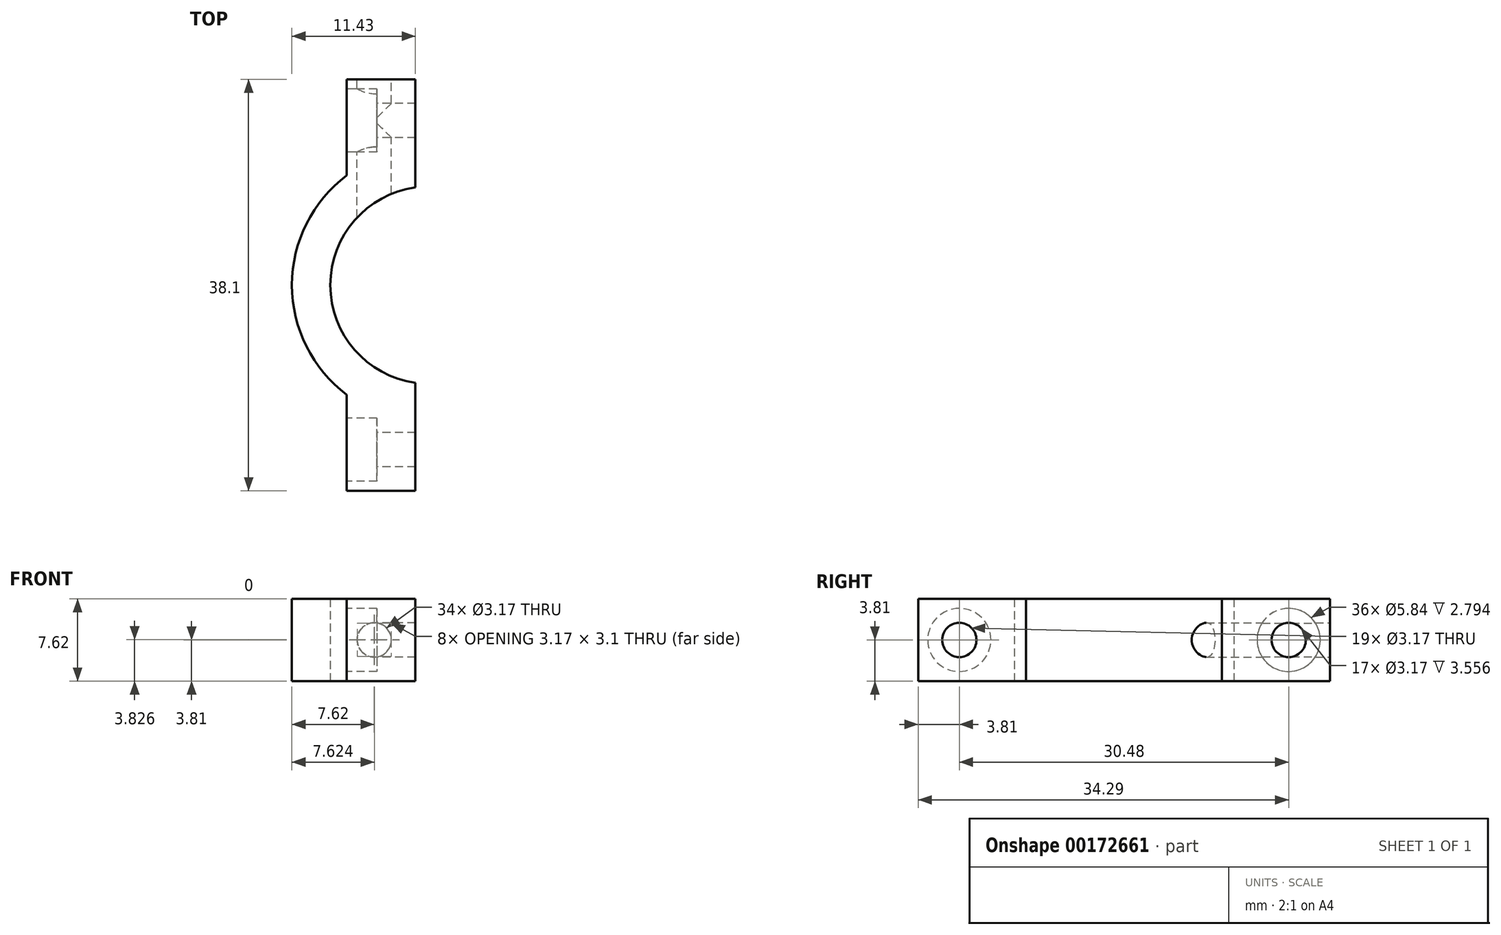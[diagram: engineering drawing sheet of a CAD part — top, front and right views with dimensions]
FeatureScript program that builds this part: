
annotation { "Feature Type Name" : "Feature", "Feature Type Description" : "" }
export const myFeature = defineFeature(function(context is Context, id is Id, definition is map)
    precondition{}
    {
        {
            var Q0;
            Q0=qCreatedBy(makeId("Top.planeOp"),FACE);
            var sketch = newSketch(context, id + "F0", { "sketchPlane" : qUnion([Q0])});
            skArc(sketch, "E0", {"start": v(12.64, 1.27) * mm, "mid": v(0, 12.7) * mm, "end": v(-12.64, 1.27) * mm});
            skArc(sketch, "E1", {"start": v(9.06, 1.27) * mm, "mid": v(0, 9.14) * mm, "end": v(-9.06, 1.27) * mm});
            skLineSegment(sketch, "E2", {"start": v(0, 9.14) * mm, "end": v(0, 12.7) * mm, "construction": true});
            skLineSegment(sketch, "E3", {"start": v(-19.05, 7.62) * mm, "end": v(-19.05, 1.27) * mm});
            skLineSegment(sketch, "E4", {"start": v(-19.05, 1.27) * mm, "end": v(-9.06, 1.27) * mm});
            skLineSegment(sketch, "E5", {"start": v(19.05, 1.27) * mm, "end": v(19.05, 7.62) * mm});
            skLineSegment(sketch, "E6", {"start": v(-19.05, 7.62) * mm, "end": v(-5.05, 7.62) * mm});
            skLineSegment(sketch, "E7", {"start": v(-11.43, 7.62) * mm, "end": v(-11.43, 1.27) * mm});
            skLineSegment(sketch, "E8", {"start": v(11.43, 7.62) * mm, "end": v(11.43, 1.27) * mm});
            skPoint(sketch, "E9.orphan", {"position": v(19.05, 12.7) * mm});
            skLineSegment(sketch, "E10.trimOffspring", {"start": v(9.06, 1.27) * mm, "end": v(19.05, 1.27) * mm});
            skPoint(sketch, "E11.orphan", {"position": v(0, -12.7) * mm});
            skLineSegment(sketch, "E12.trimOffspring", {"start": v(5.05, 7.62) * mm, "end": v(19.05, 7.62) * mm});
            skSolve(sketch);
        }
        {
            var Q0;
            Q0=qSketchRegion(id+"F0",true);
            extrude(context, id + "F1", {"entities" : qUnion([Q0]), "depth" : 7.62 * mm});
        }
        {
            var Q0;
            {var subQ0=sQuery(id+"F0.wireOp",EDGE,"E6");var subQ1=makeQuery(id+"F0.imprint","INTERSECT",VERTEX,{"derivedFrom":[subQ0,sQuery(id+"F0.wireOp",EDGE,"E8")]});Q0=makeQuery(id+"F1.opExtrude","SWEPT_FACE",FACE,{"disambiguationData":[OSD([subQ0]),TDD([makeQuery(id+"F0.imprint","IMPRINT",EDGE,{"disambiguationData":[TD([[subQ1,1.0]])],"derivedFrom":subQ0}),makeQuery(id+"F0.imprint","IMPRINT",EDGE,{"disambiguationData":[TD([[makeQuery(id+"F0.imprint","INTERSECT",VERTEX,{"derivedFrom":[sQuery(id+"F0.wireOp",EDGE,"E5"),subQ0]}),1.0]])],"derivedFrom":subQ0})])]});}
            var sketch = newSketch(context, id + "F2", { "sketchPlane" : qUnion([Q0])});
            skCircle(sketch, "E13", {"center": v(-15.24, 3.81) * mm, "radius": 2.92 * mm});
            skPoint(sketch, "E13.centerSnap0", {"position": v(10.16, 3.81) * mm});
            skCircle(sketch, "E14", {"center": v(-15.24, 3.81) * mm, "radius": 1.59 * mm});
            skSolve(sketch);
        }
        {
            var Q0;
            {var subQ0=sQuery(id+"F0.wireOp",EDGE,"E6");var subQ1=makeQuery(id+"F0.imprint","INTERSECT",VERTEX,{"derivedFrom":[subQ0,sQuery(id+"F0.wireOp",EDGE,"E7")]});Q0=makeQuery(id+"F1.opExtrude","SWEPT_FACE",FACE,{"disambiguationData":[OSD([subQ0]),TDD([makeQuery(id+"F0.imprint","IMPRINT",EDGE,{"disambiguationData":[TD([[makeQuery(id+"F0.imprint","INTERSECT",VERTEX,{"derivedFrom":[sQuery(id+"F0.wireOp",EDGE,"E3"),subQ0]}),-1.0]])],"derivedFrom":subQ0}),makeQuery(id+"F0.imprint","IMPRINT",EDGE,{"disambiguationData":[TD([[subQ1,-1.0]])],"derivedFrom":subQ0})])]});}
            var sketch = newSketch(context, id + "F3", { "sketchPlane" : qUnion([Q0])});
            skCircle(sketch, "E15", {"center": v(15.24, 3.81) * mm, "radius": 1.59 * mm});
            skPoint(sketch, "E15.centerSnap0", {"position": v(19.05, 3.81) * mm});
            skCircle(sketch, "E16", {"center": v(15.24, 3.81) * mm, "radius": 2.92 * mm});
            skSolve(sketch);
        }
        {
            var Q0;
            Q0=makeQuery(id+"F2.imprint","IMPRINT",FACE,{"disambiguationData":[TD([[makeQuery(id+"F2.imprint","IMPRINT",EDGE,{"derivedFrom":sQuery(id+"F2.wireOp",EDGE,"E14")}),1.0]])]});
            var Q1;
            Q1=makeQuery(id+"F3.imprint","IMPRINT",FACE,{"disambiguationData":[TD([[makeQuery(id+"F3.imprint","IMPRINT",EDGE,{"derivedFrom":sQuery(id+"F3.wireOp",EDGE,"E15")}),1.0]])]});
            extrude(context, id + "F4", {"entities" : qUnion([Q0, Q1]), "operationType" : NewBodyOperationType.REMOVE, "oppositeDirection" : true, "depth" : 25.4 * mm});
        }
        {
            var Q0;
            Q0=makeQuery(id+"F2.imprint","IMPRINT",FACE,{"disambiguationData":[TD([[makeQuery(id+"F2.imprint","IMPRINT",EDGE,{"derivedFrom":sQuery(id+"F2.wireOp",EDGE,"E13")}),1.0]])]});
            var Q1;
            Q1=makeQuery(id+"F3.imprint","IMPRINT",FACE,{"disambiguationData":[TD([[makeQuery(id+"F3.imprint","IMPRINT",EDGE,{"derivedFrom":sQuery(id+"F3.wireOp",EDGE,"E15")}),-1.0]])]});
            extrude(context, id + "F5", {"entities" : qUnion([Q0, Q1]), "operationType" : NewBodyOperationType.REMOVE, "oppositeDirection" : true, "depth" : 2.8 * mm});
        }
        {
            var Q0;
            Q0=makeQuery(id+"F1.opExtrude","SWEPT_BODY",BODY,{"disambiguationData":[OSD([sQuery(id+"F0.wireOp",EDGE,"E0"),sQuery(id+"F0.wireOp",EDGE,"E1"),sQuery(id+"F0.wireOp",EDGE,"E3"),sQuery(id+"F0.wireOp",EDGE,"E4"),sQuery(id+"F0.wireOp",EDGE,"E5"),sQuery(id+"F0.wireOp",EDGE,"E6"),sQuery(id+"F0.wireOp",EDGE,"E10.trimOffspring"),sQuery(id+"F0.wireOp",EDGE,"E12.trimOffspring")])]});
            var Q1;
            Q1=makeQuery(id+"F1.opExtrude","SWEPT_EDGE",EDGE,{"disambiguationData":[OSD([sQuery(id+"F0.wireOp",EDGE,"E5"),sQuery(id+"F0.wireOp",EDGE,"E10.trimOffspring")])]});
            var Q2;
            Q2=makeQuery(id+"F1.opExtrude","SWEPT_EDGE",EDGE,{"disambiguationData":[OSD([sQuery(id+"F0.wireOp",EDGE,"E5"),sQuery(id+"F0.wireOp",EDGE,"E10.trimOffspring")])]});
            transform(context, id + "F6", {"entities" : qUnion([Q0]), "transformType" : TransformType.ROTATION, "transformAxis" : qUnion([Q2]), "angle" : 90 * degree, "oppositeDirection" : true, "makeCopy" : false});
        }
    });
